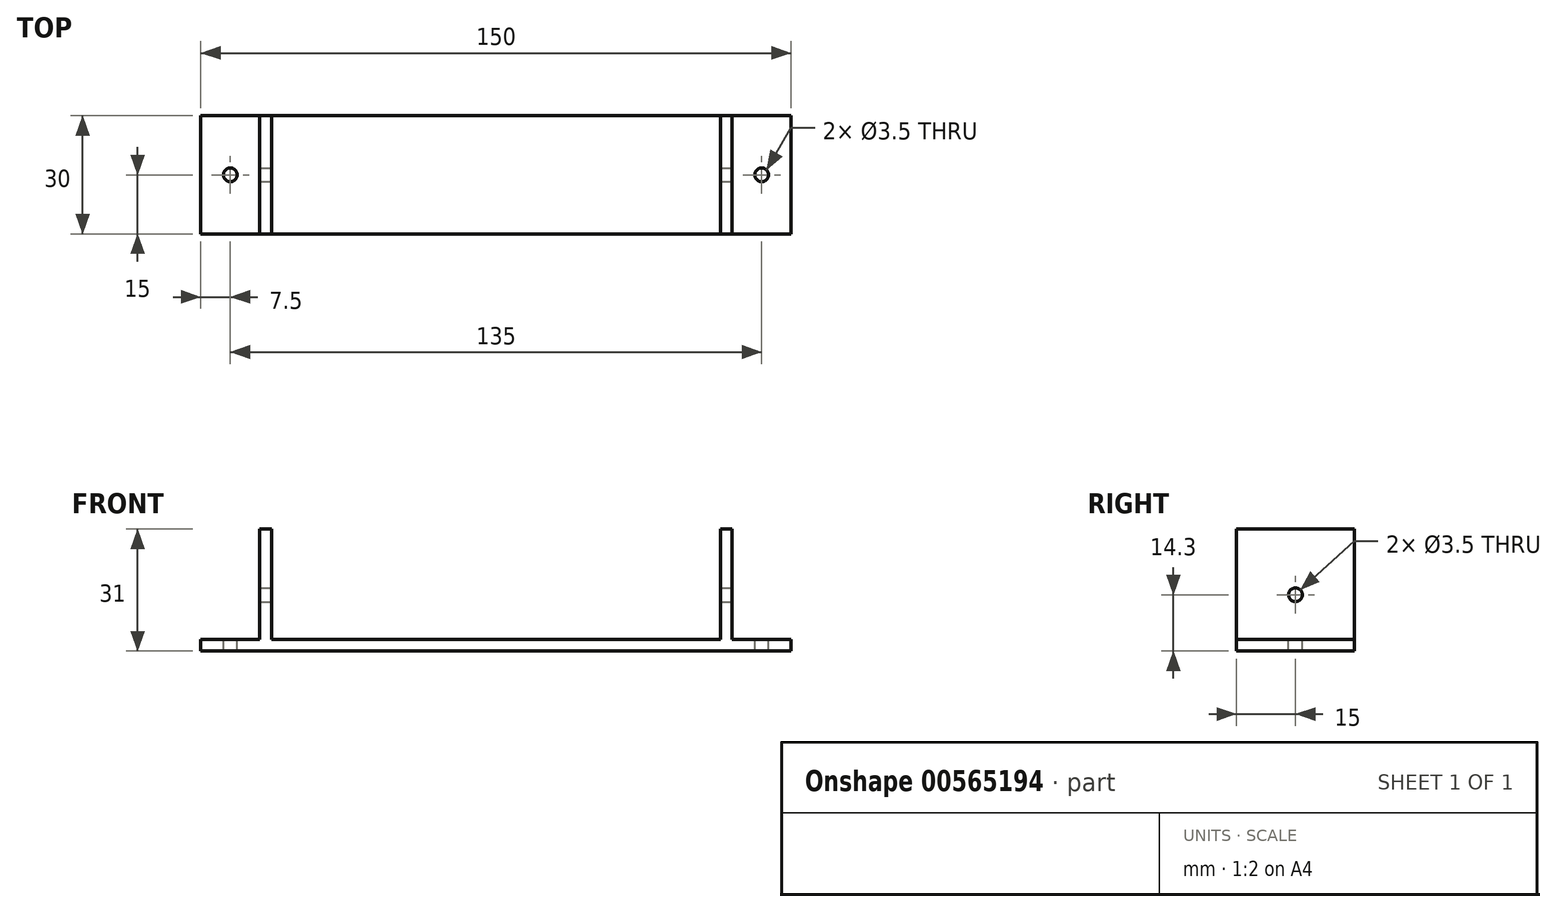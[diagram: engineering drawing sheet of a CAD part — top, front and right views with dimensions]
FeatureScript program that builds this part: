
annotation { "Feature Type Name" : "Feature", "Feature Type Description" : "" }
export const myFeature = defineFeature(function(context is Context, id is Id, definition is map)
    precondition{}
    {
        {
            var Q0;
            Q0=qCreatedBy(makeId("Top.planeOp"),FACE);
            var sketch = newSketch(context, id + "F0", { "sketchPlane" : qUnion([Q0])});
            skLineSegment(sketch, "E0.bottom", {"start": v(0, 0) * mm, "end": v(114, 0) * mm});
            skLineSegment(sketch, "E0.top", {"start": v(0, 30) * mm, "end": v(114, 30) * mm});
            skLineSegment(sketch, "E0.left", {"start": v(0, 0) * mm, "end": v(0, 30) * mm});
            skLineSegment(sketch, "E0.right", {"start": v(114, 0) * mm, "end": v(114, 30) * mm});
            skLineSegment(sketch, "E1.bottom", {"start": v(0, 30) * mm, "end": v(-3, 30) * mm});
            skLineSegment(sketch, "E1.top", {"start": v(0, 0) * mm, "end": v(-3, 0) * mm});
            skLineSegment(sketch, "E1.left", {"start": v(0, 30) * mm, "end": v(0, 0) * mm});
            skLineSegment(sketch, "E1.right", {"start": v(-3, 30) * mm, "end": v(-3, 0) * mm});
            skLineSegment(sketch, "E2.bottom", {"start": v(114, 0) * mm, "end": v(117, 0) * mm});
            skLineSegment(sketch, "E2.top", {"start": v(114, 30) * mm, "end": v(117, 30) * mm});
            skLineSegment(sketch, "E2.right", {"start": v(117, 0) * mm, "end": v(117, 30) * mm});
            skLineSegment(sketch, "E3.bottom", {"start": v(-3, 30) * mm, "end": v(-18, 30) * mm});
            skLineSegment(sketch, "E3.top", {"start": v(-3, 0) * mm, "end": v(-18, 0) * mm});
            skLineSegment(sketch, "E3.right", {"start": v(-18, 30) * mm, "end": v(-18, 0) * mm});
            skLineSegment(sketch, "E4", {"start": v(-18, 30) * mm, "end": v(-3, 0) * mm, "construction": true});
            skCircle(sketch, "E5", {"center": v(-10.5, 15) * mm, "radius": 1.75 * mm});
            skLineSegment(sketch, "E6", {"start": v(57, 30) * mm, "end": v(57, 0) * mm, "construction": true});
            skLineSegment(sketch, "E7.MirrorCS", {"start": v(132, 30) * mm, "end": v(132, 0) * mm});
            skCircle(sketch, "E8.MirrorC", {"center": v(124.5, 15) * mm, "radius": 1.75 * mm});
            skLineSegment(sketch, "E9.MirrorCS", {"start": v(117, 0) * mm, "end": v(132, 0) * mm});
            skLineSegment(sketch, "E10.MirrorCS", {"start": v(117, 30) * mm, "end": v(132, 30) * mm});
            skSolve(sketch);
        }
        {
            var Q0;
            Q0=makeQuery(id+"F0.imprint","IMPRINT",FACE,{"disambiguationData":[TD([[makeQuery(id+"F0.imprint","IMPRINT",EDGE,{"derivedFrom":sQuery(id+"F0.wireOp",EDGE,"E1.bottom")}),1.0]])]});
            var Q1;
            Q1=makeQuery(id+"F0.imprint","IMPRINT",FACE,{"disambiguationData":[TD([[makeQuery(id+"F0.imprint","IMPRINT",EDGE,{"derivedFrom":sQuery(id+"F0.wireOp",EDGE,"E0.bottom")}),1.0]])]});
            var Q2;
            Q2=makeQuery(id+"F0.imprint","IMPRINT",FACE,{"disambiguationData":[TD([[makeQuery(id+"F0.imprint","IMPRINT",EDGE,{"derivedFrom":sQuery(id+"F0.wireOp",EDGE,"E2.bottom")}),1.0]])]});
            extrude(context, id + "F1", {"entities" : qUnion([Q0, Q1, Q2]), "depth" : -3 * mm, "offsetDistance" : 25 * mm});
        }
        {
            var Q0;
            Q0=makeQuery(id+"F0.imprint","IMPRINT",FACE,{"disambiguationData":[TD([[makeQuery(id+"F0.imprint","IMPRINT",EDGE,{"derivedFrom":sQuery(id+"F0.wireOp",EDGE,"E1.bottom")}),1.0]])]});
            var Q1;
            Q1=makeQuery(id+"F0.imprint","IMPRINT",FACE,{"disambiguationData":[TD([[makeQuery(id+"F0.imprint","IMPRINT",EDGE,{"derivedFrom":sQuery(id+"F0.wireOp",EDGE,"E2.bottom")}),1.0]])]});
            extrude(context, id + "F2", {"entities" : qUnion([Q0, Q1]), "operationType" : NewBodyOperationType.ADD, "depth" : 28 * mm, "offsetDistance" : 25 * mm});
        }
        {
            var Q0;
            Q0=makeQuery(id+"F0.imprint","IMPRINT",FACE,{"disambiguationData":[TD([[makeQuery(id+"F0.imprint","IMPRINT",EDGE,{"derivedFrom":sQuery(id+"F0.wireOp",EDGE,"E3.bottom")}),1.0]])]});
            var Q1;
            Q1=makeQuery(id+"F0.imprint","IMPRINT",FACE,{"disambiguationData":[TD([[makeQuery(id+"F0.imprint","IMPRINT",EDGE,{"derivedFrom":sQuery(id+"F0.wireOp",EDGE,"E2.right")}),-1.0]])]});
            extrude(context, id + "F3", {"entities" : qUnion([Q0, Q1]), "operationType" : NewBodyOperationType.ADD, "depth" : -3 * mm, "offsetDistance" : 25 * mm});
        }
        {
            var Q0;
            {var subQ0=sQuery(id+"F0.wireOp",EDGE,"E2.right");Q0=makeQuery(id+"F2.boolean.opBoolean","MERGE",FACE,{"derivedFrom":[makeQuery(id+"F1.opExtrude","SWEPT_FACE",FACE,{"disambiguationData":[OSD([subQ0])]}),makeQuery(id+"F2.opExtrude","SWEPT_FACE",FACE,{"disambiguationData":[OSD([subQ0])]})]});}
            var sketch = newSketch(context, id + "F4", { "sketchPlane" : qUnion([Q0])});
            skLineSegment(sketch, "E11", {"start": v(15, 0) * mm, "end": v(15, 11) * mm, "construction": true});
            skCircle(sketch, "E12", {"center": v(15, 11.3) * mm, "radius": 1.75 * mm});
            skSolve(sketch);
        }
        {
            var Q0;
            Q0=makeQuery(id+"F4.imprint","IMPRINT",FACE,{"disambiguationData":[TD([[makeQuery(id+"F4.imprint","IMPRINT",EDGE,{"derivedFrom":sQuery(id+"F4.wireOp",EDGE,"E12")}),1.0]])]});
            extrude(context, id + "F5", {"entities" : qUnion([Q0]), "operationType" : NewBodyOperationType.REMOVE, "oppositeDirection" : true, "depth" : 200 * mm, "offsetDistance" : 25 * mm});
        }
    });
